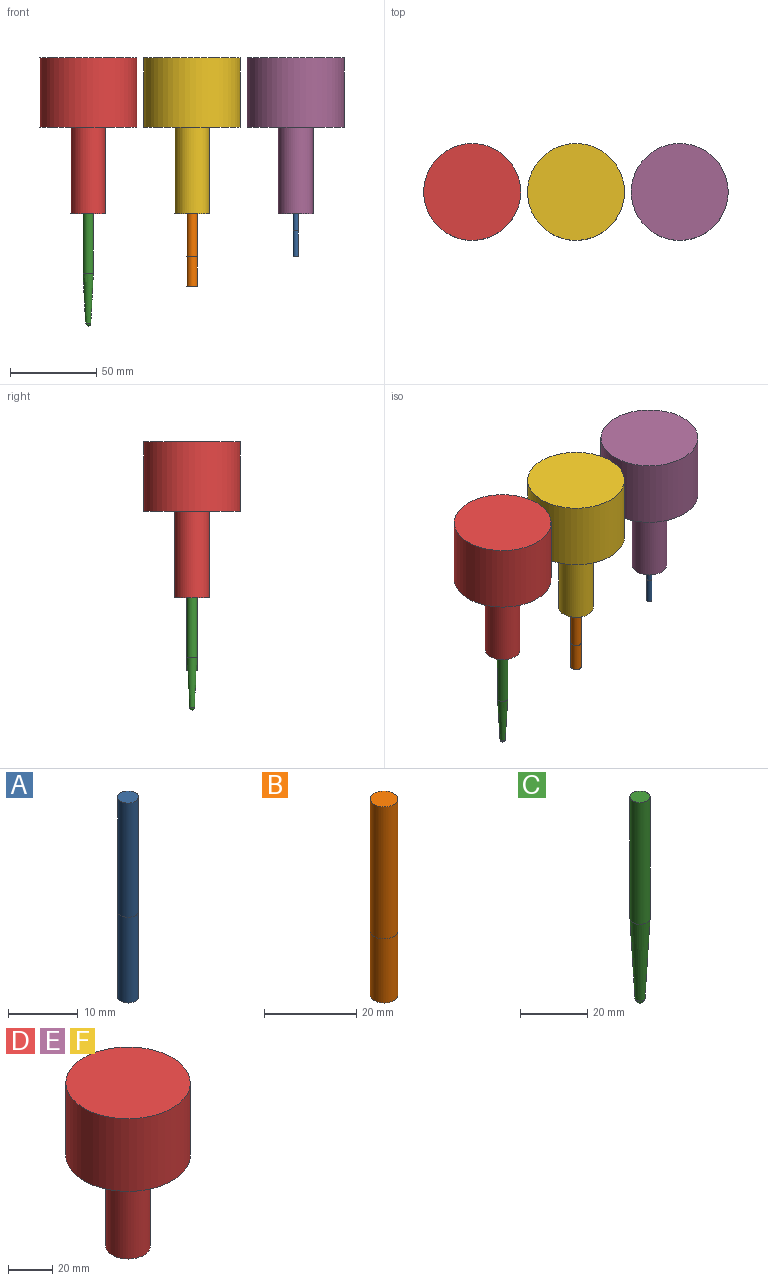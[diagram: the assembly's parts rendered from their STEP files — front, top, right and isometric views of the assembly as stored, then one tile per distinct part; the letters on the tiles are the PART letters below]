
ASSEMBLY  parts=6 mates=5
PART A: 4 faces, bbox 3x3x35 mm
  f0: cylinder r=1.5mm len=15mm, axis (0,0,1), area 141.4mm2, adj f2,f3
  f1: plane 3x3mm, normal (0,0,1), area 7.1mm2, adj f2
  f2: cylinder r=1.5mm len=20mm, axis (0,0,1), area 188.5mm2, adj f0,f1
  f3: plane 3x3mm, normal (0,0,-1), area 7.1mm2, adj f0
PART B: 4 faces, bbox 6x6x52 mm
  f0: cylinder r=3mm len=17mm, axis (0,0,1), area 320.4mm2, adj f2,f3
  f1: plane 6x6mm, normal (0,0,1), area 28.3mm2, adj f2
  f2: cylinder r=3mm len=35mm, axis (0,0,1), area 659.7mm2, adj f0,f1
  f3: plane 6x6mm, normal (0,0,-1), area 28.3mm2, adj f0
PART C: 4 faces, bbox 6x6x75 mm
  f0: cylinder r=3mm len=44.5mm, axis (0,0,1), area 838.8mm2, adj f1,f3
  f1: cone r=1.5mm half-angle=3deg, axis (0,0,1), area 411.4mm2, adj f0,f2
  f2: sphere r=1.5mm, area 13.4mm2, adj f1
  f3: plane 6x6mm, normal (0,0,1), area 28.3mm2, adj f0
PART D: 7 faces, bbox 56x56x90 mm
  f0: plane 20x20mm, normal (0,0,-1), area 285.9mm2, adj f1,f6
  f1: cylinder r=3mm len=10mm, axis (0,0,1), area 188.5mm2, adj f0,f2
  f2: plane 6x6mm, normal (0,0,-1), area 28.3mm2, adj f1
  f3: plane 56x56mm, normal (0,0,1), area 2463mm2, adj f4
  f4: cylinder r=28mm len=56mm, axis (0,0,1), area 7037.2mm2, adj f3,f5
  f5: plane 56x56mm, normal (0,0,-1), area 2148.8mm2, adj f4,f6
  f6: cylinder r=10mm len=50mm, axis (0,0,1), area 3141.6mm2, adj f0,f5
PART E: same geometry as D
PART F: same geometry as D
PLACE A t=(41.3,-37.5,9.6)mm
PLACE B t=(-18.7,-37.5,9.6)mm
PLACE C t=(-78.7,-37.5,9.6)mm
PLACE D t=(-78.7,-37.5,9.6)mm fixed
PLACE E t=(41.3,-37.5,9.6)mm
PLACE F t=(-18.7,-37.5,9.6)mm
MATE planar E.f1 <-> D.f1  axis (0,0,1) through (41.3,-37.5,164.6)mm
MATE planar F.f1 <-> E.f1  axis (0,0,1) through (-18.7,-37.5,164.6)mm
MATE fastened F.f1 <-> B.f0  axis (0,0,-1) through (-18.7,-37.5,84.6)mm
MATE fastened E.f1 <-> A.f0  axis (0,0,-1) through (41.3,-37.5,84.6)mm
MATE fastened D.f1 <-> C.f0  axis (0,0,-1) through (-78.7,-37.5,84.6)mm
